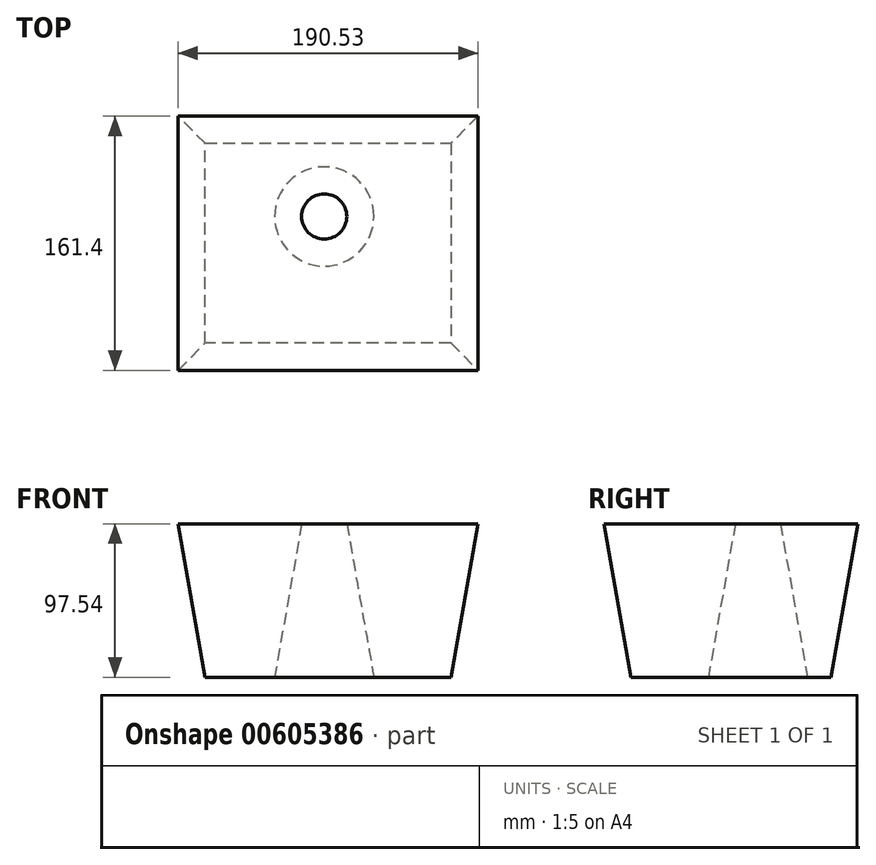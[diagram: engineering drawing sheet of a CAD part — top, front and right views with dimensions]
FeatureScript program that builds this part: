
annotation { "Feature Type Name" : "Feature", "Feature Type Description" : "" }
export const myFeature = defineFeature(function(context is Context, id is Id, definition is map)
    precondition{}
    {
        {
            var Q0;
            Q0=qCreatedBy(makeId("Top.planeOp"),FACE);
            var sketch = newSketch(context, id + "F0", { "sketchPlane" : qUnion([Q0])});
            skLineSegment(sketch, "E0.bottom", {"start": v(-67.59, 65.17) * mm, "end": v(88.54, 65.17) * mm});
            skLineSegment(sketch, "E0.top", {"start": v(-67.59, -61.83) * mm, "end": v(88.54, -61.83) * mm});
            skLineSegment(sketch, "E0.left", {"start": v(-67.59, 65.17) * mm, "end": v(-67.59, -61.83) * mm});
            skLineSegment(sketch, "E0.right", {"start": v(88.54, 65.17) * mm, "end": v(88.54, -61.83) * mm});
            skCircle(sketch, "E1", {"center": v(8.03, 18.66) * mm, "radius": 31.52 * mm});
            skSolve(sketch);
        }
        {
            var Q0;
            Q0 = qSketchRegion(id + "F0", true);
            extrude(context, id + "F1", {"entities" : qUnion([Q0]), "depth" : 97.54 * mm, "offsetDistance" : 25.4 * mm, "hasDraft" : true, "draftAngle" : 10 * degree});
        }
    });
